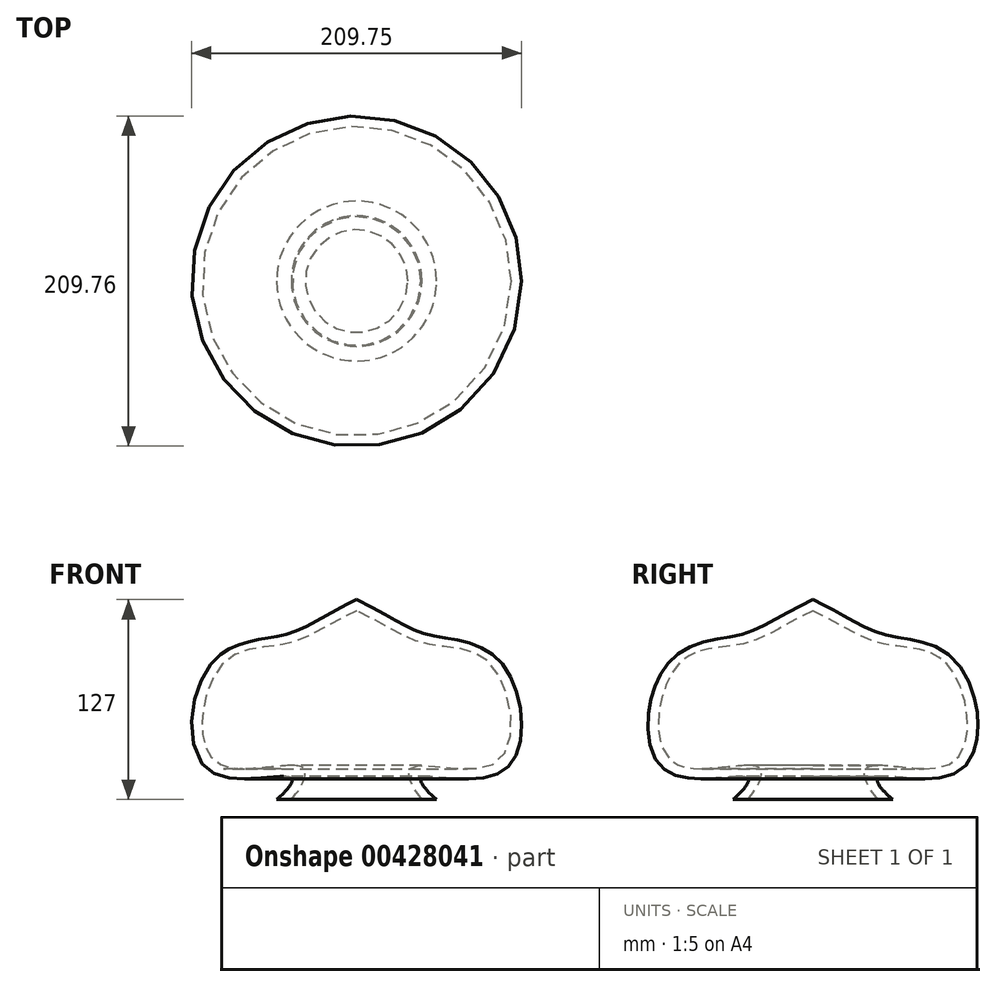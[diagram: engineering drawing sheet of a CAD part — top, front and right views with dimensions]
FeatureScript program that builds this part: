
annotation { "Feature Type Name" : "Feature", "Feature Type Description" : "" }
export const myFeature = defineFeature(function(context is Context, id is Id, definition is map)
    precondition{}
    {
        {
            var Q0;
            Q0=qCreatedBy(makeId("Front.planeOp"),FACE);
            var sketch = newSketch(context, id + "F0", { "sketchPlane" : qUnion([Q0])});
            skFitSpline(sketch, "E0", {"points": [v(50.8, 0) * mm, v(41.65, 13.79) * mm, v(93.52, 18.42) * mm, v(92.13, 86.6) * mm, v(45.68, 104.78) * mm, v(0, 127) * mm], "startDerivative": vector(-159.48, 138.45) * mm, "endDerivative": vector(-333.85, 158) * mm});
            skFitSpline(sketch, "E1", {"points": [v(41.47, 0) * mm, v(34.33, 20.33) * mm, v(89.04, 23.9) * mm, v(85.47, 85.74) * mm, v(44.64, 98.82) * mm, v(0, 119.83) * mm], "startDerivative": vector(-136.72, 156.26) * mm, "endDerivative": vector(-269.94, 124.73) * mm});
            skLineSegment(sketch, "E2", {"start": v(0, 119.83) * mm, "end": v(0, 127) * mm});
            skLineSegment(sketch, "E3", {"start": v(41.47, 0) * mm, "end": v(50.8, 0) * mm});
            skSolve(sketch);
        }
        {
            var Q0;
            Q0=makeQuery(id+"F0.imprint","IMPRINT",FACE,{"disambiguationData":[TD([[makeQuery(id+"F0.imprint","IMPRINT",EDGE,{"derivedFrom":sQuery(id+"F0.wireOp",EDGE,"E0")}),1.0]])]});
            var Q1;
            Q1=sQuery(id+"F0.wireOp",EDGE,"E2");
            revolve(context, id + "F1", {"entities" : qUnion([Q0]), "axis" : qUnion([Q1]), "revolveType" : RevolveType.FULL});
        }
    });
